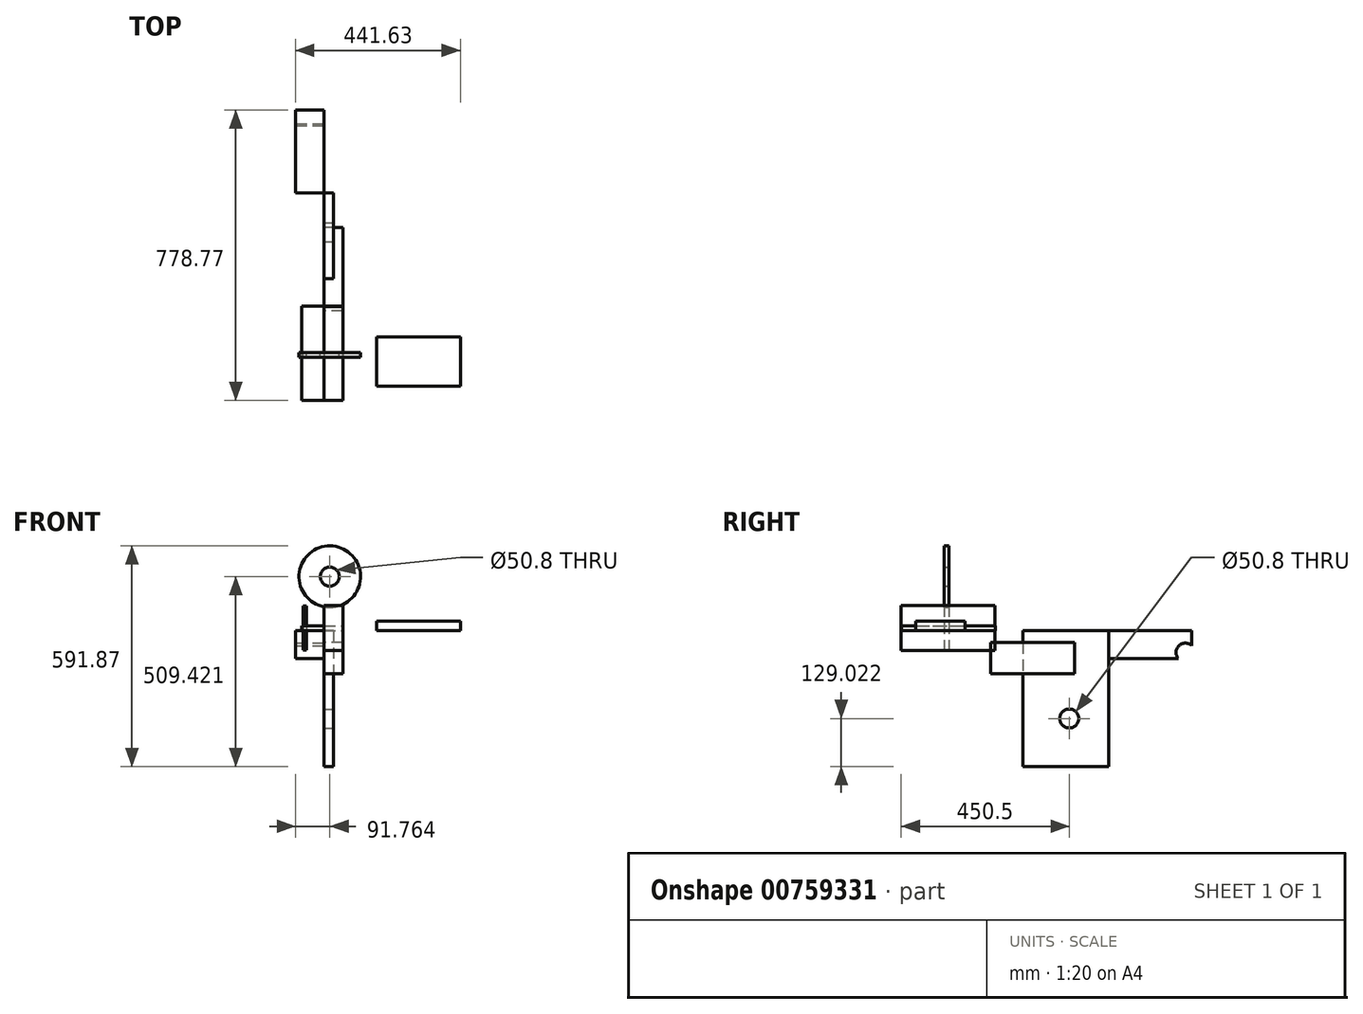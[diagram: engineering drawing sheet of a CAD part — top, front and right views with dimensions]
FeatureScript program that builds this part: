
annotation { "Feature Type Name" : "Feature", "Feature Type Description" : "" }
export const myFeature = defineFeature(function(context is Context, id is Id, definition is map)
    precondition{}
    {
        {
            var Q0;
            Q0=qCreatedBy(makeId("Right.planeOp"),FACE);
            var sketch = newSketch(context, id + "F0", { "sketchPlane" : qUnion([Q0])});
            skLineSegment(sketch, "E0.bottom", {"start": v(123.96, 66.67) * mm, "end": v(-127.95, 66.67) * mm});
            skLineSegment(sketch, "E0.top", {"start": v(123.96, -53.74) * mm, "end": v(-127.95, -53.74) * mm});
            skLineSegment(sketch, "E0.left", {"start": v(123.96, 66.67) * mm, "end": v(123.96, -53.74) * mm});
            skLineSegment(sketch, "E0.right", {"start": v(-127.95, 66.67) * mm, "end": v(-127.95, -53.74) * mm});
            skSolve(sketch);
        }
        {
            var Q0;
            Q0=makeQuery(id+"F0.imprint","IMPRINT",FACE,{"disambiguationData":[TD([[makeQuery(id+"F0.imprint","IMPRINT",EDGE,{"derivedFrom":sQuery(id+"F0.wireOp",EDGE,"E0.bottom")}),1.0]])]});
            extrude(context, id + "F1", {"entities" : qUnion([Q0]), "depth" : 50.8 * mm, "offsetDistance" : 25.4 * mm});
        }
        {
            var Q0;
            Q0=qCreatedBy(makeId("Front.planeOp"),FACE);
            var sketch = newSketch(context, id + "F2", { "sketchPlane" : qUnion([Q0])});
            skLineSegment(sketch, "E1.bottom", {"start": v(-46.48, 66.05) * mm, "end": v(-56.27, 66.05) * mm});
            skLineSegment(sketch, "E1.top", {"start": v(-46.48, -52.52) * mm, "end": v(-56.27, -52.52) * mm});
            skLineSegment(sketch, "E1.left", {"start": v(-46.48, 66.05) * mm, "end": v(-46.48, -52.52) * mm});
            skLineSegment(sketch, "E1.right", {"start": v(-56.27, 66.05) * mm, "end": v(-56.27, -52.52) * mm});
            skSolve(sketch);
        }
        {
            var Q0;
            Q0=makeQuery(id+"F2.imprint","IMPRINT",FACE,{"disambiguationData":[TD([[makeQuery(id+"F2.imprint","IMPRINT",EDGE,{"derivedFrom":sQuery(id+"F2.wireOp",EDGE,"E1.bottom")}),1.0]])]});
            extrude(context, id + "F3", {"entities" : qUnion([Q0]), "depth" : 12.7 * mm, "offsetDistance" : 25.4 * mm});
        }
        {
            var Q0;
            Q0=qCreatedBy(makeId("Front.planeOp"),FACE);
            var sketch = newSketch(context, id + "F4", { "sketchPlane" : qUnion([Q0])});
            skArc(sketch, "E2", {"start": v(-50.02, 64.15) * mm, "mid": v(37.27, 58.21) * mm, "end": v(-28.8, 115.56) * mm});
            skCircle(sketch, "E3", {"center": v(15.56, 144.3) * mm, "radius": 82.45 * mm});
            skSolve(sketch);
        }
        {
            var Q0;
            Q0 = qSketchRegion(id + "F4", true);
            extrude(context, id + "F5", {"entities" : qUnion([Q0]), "depth" : 12.7 * mm, "offsetDistance" : 25.4 * mm});
        }
        {
            var Q0;
            Q0=qCreatedBy(makeId("Top.planeOp"),FACE);
            var sketch = newSketch(context, id + "F6", { "sketchPlane" : qUnion([Q0])});
            skLineSegment(sketch, "E4.bottom", {"start": v(-59.14, -127.5) * mm, "end": v(50.86, -127.5) * mm});
            skLineSegment(sketch, "E4.top", {"start": v(-59.14, 124.15) * mm, "end": v(50.86, 124.15) * mm});
            skLineSegment(sketch, "E4.left", {"start": v(-59.14, -127.5) * mm, "end": v(-59.14, 124.15) * mm});
            skLineSegment(sketch, "E4.right", {"start": v(50.86, -127.5) * mm, "end": v(50.86, 124.15) * mm});
            skSolve(sketch);
        }
        {
            var Q0;
            Q0 = qSketchRegion(id + "F6", true);
            extrude(context, id + "F7", {"entities" : qUnion([Q0]), "depth" : 12.7 * mm, "offsetDistance" : 25.4 * mm});
        }
        {
            var Q0;
            Q0=makeQuery(id+"F5.opExtrude","CAP_FACE",FACE,{"disambiguationData":[OSD([sQuery(id+"F4.wireOp",EDGE,"E3")])],"isStart":true});
            var sketch = newSketch(context, id + "F8", { "sketchPlane" : qUnion([Q0])});
            skPoint(sketch, "E5", {"position": v(-15.56, 144.3) * mm});
            skSolve(sketch);
        }
        {
            var Q0;
            Q0=sQuery(id+"F8.wireOp",VERTEX,"E5");
            var Q1;
            Q1=makeQuery(id+"F5.opExtrude","SWEPT_BODY",BODY,{"disambiguationData":[OSD([sQuery(id+"F4.wireOp",EDGE,"E3")])]});
            hole(context, id + "F9", {"style" : HoleStyle.SIMPLE, "endStyle" : HoleEndStyle.THROUGH, "holeDiameter" : 50.8 * mm, "majorDiameter" : 6.35 * mm, "isTappedThrough" : true, "tappedDepth" : 12.7 * mm, "tapClearance" : 3, "locations" : qUnion([Q0]), "scope" : qUnion([Q1])});
        }
        {
            var Q0;
            Q0=qCreatedBy(makeId("Top.planeOp"),FACE);
            var sketch = newSketch(context, id + "F10", { "sketchPlane" : qUnion([Q0])});
            skLineSegment(sketch, "E6.bottom", {"start": v(140.9, -89.27) * mm, "end": v(365.43, -89.27) * mm});
            skLineSegment(sketch, "E6.top", {"start": v(140.9, 42.8) * mm, "end": v(365.43, 42.8) * mm});
            skLineSegment(sketch, "E6.left", {"start": v(140.9, -89.27) * mm, "end": v(140.9, 42.8) * mm});
            skLineSegment(sketch, "E6.right", {"start": v(365.43, -89.27) * mm, "end": v(365.43, 42.8) * mm});
            skSolve(sketch);
        }
        {
            var Q0;
            Q0=makeQuery(id+"F10.imprint","IMPRINT",FACE,{"disambiguationData":[TD([[makeQuery(id+"F10.imprint","IMPRINT",EDGE,{"derivedFrom":sQuery(id+"F10.wireOp",EDGE,"E6.bottom")}),1.0]])]});
            extrude(context, id + "F11", {"entities" : qUnion([Q0]), "depth" : 25.4 * mm, "offsetDistance" : 25.4 * mm});
        }
        {
            var Q0;
            Q0=qCreatedBy(makeId("Right.planeOp"),FACE);
            var sketch = newSketch(context, id + "F12", { "sketchPlane" : qUnion([Q0])});
            skLineSegment(sketch, "E7.bottom", {"start": v(198.26, 0) * mm, "end": v(427.9, 0) * mm});
            skLineSegment(sketch, "E7.top", {"start": v(198.26, -365.13) * mm, "end": v(427.9, -365.13) * mm});
            skLineSegment(sketch, "E7.left", {"start": v(198.26, 0) * mm, "end": v(198.26, -365.13) * mm});
            skLineSegment(sketch, "E7.right", {"start": v(427.9, 0) * mm, "end": v(427.9, -365.13) * mm});
            skSolve(sketch);
        }
        {
            var Q0;
            Q0=makeQuery(id+"F12.imprint","IMPRINT",FACE,{"disambiguationData":[TD([[makeQuery(id+"F12.imprint","IMPRINT",EDGE,{"derivedFrom":sQuery(id+"F12.wireOp",EDGE,"E7.bottom")}),-1.0]])]});
            extrude(context, id + "F13", {"entities" : qUnion([Q0]), "depth" : 25.4 * mm, "offsetDistance" : 25.4 * mm});
        }
        {
            var Q0;
            Q0=qCreatedBy(makeId("Front.planeOp"),FACE);
            var sketch = newSketch(context, id + "F14", { "sketchPlane" : qUnion([Q0])});
            skArc(sketch, "E8", {"start": v(230.25, 28.07) * mm, "mid": v(123.09, 214.87) * mm, "end": v(38.83, 16.68) * mm});
            skSolve(sketch);
        }
        {
            var Q0;
            Q0=sQuery(id+"F14.wireOp",EDGE,"E8");
            extrude(context, id + "F15", {"bodyType" : ToolBodyType.SURFACE, "surfaceEntities" : qUnion([Q0]), "depth" : 50.8 * mm, "offsetDistance" : 25.4 * mm});
        }
        {
            var Q0;
            Q0=qCreatedBy(makeId("Front.planeOp"),FACE);
            var sketch = newSketch(context, id + "F16", { "sketchPlane" : qUnion([Q0])});
            skArc(sketch, "E9", {"start": v(19.56, 54.99) * mm, "mid": v(-174.04, -384) * mm, "end": v(113.6, 0) * mm});
            skSolve(sketch);
        }
        {
            var Q0;
            Q0=sQuery(id+"F16.wireOp",EDGE,"E9");
            extrude(context, id + "F17", {"bodyType" : ToolBodyType.SURFACE, "surfaceEntities" : qUnion([Q0]), "endBound" : BoundingType.SYMMETRIC, "depth" : 254 * mm, "offsetDistance" : 25.4 * mm});
        }
        {
            var Q0;
            Q0=qCreatedBy(makeId("Right.planeOp"),FACE);
            var sketch = newSketch(context, id + "F18", { "sketchPlane" : qUnion([Q0])});
            skLineSegment(sketch, "E10.bottom", {"start": v(112.33, -32.4) * mm, "end": v(336.19, -32.4) * mm});
            skLineSegment(sketch, "E10.top", {"start": v(112.33, -115.73) * mm, "end": v(336.19, -115.73) * mm});
            skLineSegment(sketch, "E10.left", {"start": v(112.33, -32.4) * mm, "end": v(112.33, -115.73) * mm});
            skLineSegment(sketch, "E10.right", {"start": v(336.19, -32.4) * mm, "end": v(336.19, -115.73) * mm});
            skSolve(sketch);
        }
        {
            var Q0;
            Q0=makeQuery(id+"F18.imprint","IMPRINT",FACE,{"disambiguationData":[TD([[makeQuery(id+"F18.imprint","IMPRINT",EDGE,{"derivedFrom":sQuery(id+"F18.wireOp",EDGE,"E10.bottom")}),-1.0]])]});
            extrude(context, id + "F19", {"entities" : qUnion([Q0]), "depth" : 50.8 * mm, "offsetDistance" : 25.4 * mm});
        }
        {
            var Q0;
            Q0=makeQuery(id+"F13.opExtrude","CAP_FACE",FACE,{"disambiguationData":[OSD([sQuery(id+"F12.wireOp",EDGE,"E7.bottom"),sQuery(id+"F12.wireOp",EDGE,"E7.top"),sQuery(id+"F12.wireOp",EDGE,"E7.left"),sQuery(id+"F12.wireOp",EDGE,"E7.right")])],"isStart":true});
            var sketch = newSketch(context, id + "F20", { "sketchPlane" : qUnion([Q0])});
            skLineSegment(sketch, "E11.bottom", {"start": v(-650.82, -75.63) * mm, "end": v(-204.96, -75.63) * mm});
            skLineSegment(sketch, "E11.top", {"start": v(-650.82, -0.05) * mm, "end": v(-204.96, -0.05) * mm});
            skLineSegment(sketch, "E11.left", {"start": v(-650.82, -75.63) * mm, "end": v(-650.82, -0.05) * mm});
            skLineSegment(sketch, "E11.right", {"start": v(-204.96, -75.63) * mm, "end": v(-204.96, -0.05) * mm});
            skPoint(sketch, "E11.middle", {"position": v(-427.9, -37.84) * mm});
            skSolve(sketch);
        }
        {
            var Q0;
            {var subQ0=sQuery(id+"F20.wireOp",EDGE,"E11.left");Q0=makeQuery(id+"F20.imprint","IMPRINT",FACE,{"disambiguationData":[TD([[makeQuery(id+"F20.imprint","IMPRINT",EDGE,{"derivedFrom":subQ0}),-1.0]])]});}
            extrude(context, id + "F21", {"entities" : qUnion([Q0]), "depth" : 76.2 * mm, "offsetDistance" : 25.4 * mm});
        }
        {
            var Q0;
            Q0=makeQuery(id+"F13.opExtrude","CAP_FACE",FACE,{"disambiguationData":[OSD([sQuery(id+"F12.wireOp",EDGE,"E7.bottom"),sQuery(id+"F12.wireOp",EDGE,"E7.top"),sQuery(id+"F12.wireOp",EDGE,"E7.left"),sQuery(id+"F12.wireOp",EDGE,"E7.right")])],"isStart":false});
            var sketch = newSketch(context, id + "F22", { "sketchPlane" : qUnion([Q0])});
            skPoint(sketch, "E12", {"position": v(322.55, -236.1) * mm});
            skSolve(sketch);
        }
        {
            var Q0;
            Q0=sQuery(id+"F22.wireOp",VERTEX,"E12");
            var Q1;
            Q1=makeQuery(id+"F13.opExtrude","SWEPT_BODY",BODY,{"disambiguationData":[OSD([sQuery(id+"F12.wireOp",EDGE,"E7.bottom"),sQuery(id+"F12.wireOp",EDGE,"E7.top"),sQuery(id+"F12.wireOp",EDGE,"E7.left"),sQuery(id+"F12.wireOp",EDGE,"E7.right")])]});
            hole(context, id + "F23", {"style" : HoleStyle.SIMPLE, "endStyle" : HoleEndStyle.THROUGH, "holeDiameter" : 50.8 * mm, "majorDiameter" : 6.35 * mm, "isTappedThrough" : true, "tappedDepth" : 12.7 * mm, "tapClearance" : 3, "locations" : qUnion([Q0]), "scope" : qUnion([Q1])});
        }
        {
            var Q0;
            Q0=makeQuery(id+"F21.opExtrude","CAP_FACE",FACE,{"disambiguationData":[OSD([sQuery(id+"F12.wireOp",EDGE,"E7.right"),sQuery(id+"F20.wireOp",EDGE,"E11.bottom"),sQuery(id+"F20.wireOp",EDGE,"E11.top"),sQuery(id+"F20.wireOp",EDGE,"E11.left")])],"isStart":true});
            var sketch = newSketch(context, id + "F24", { "sketchPlane" : qUnion([Q0])});
            skPoint(sketch, "E13", {"position": v(633.74, -59.33) * mm});
            skSolve(sketch);
        }
        {
            var Q0;
            Q0=sQuery(id+"F24.wireOp",VERTEX,"E13");
            var Q1;
            Q1=makeQuery(id+"F21.opExtrude","SWEPT_BODY",BODY,{"disambiguationData":[OSD([sQuery(id+"F12.wireOp",EDGE,"E7.right"),sQuery(id+"F20.wireOp",EDGE,"E11.bottom"),sQuery(id+"F20.wireOp",EDGE,"E11.top"),sQuery(id+"F20.wireOp",EDGE,"E11.left")])]});
            hole(context, id + "F25", {"style" : HoleStyle.SIMPLE, "endStyle" : HoleEndStyle.THROUGH, "holeDiameter" : 50.8 * mm, "majorDiameter" : 6.35 * mm, "isTappedThrough" : true, "tappedDepth" : 12.7 * mm, "tapClearance" : 3, "locations" : qUnion([Q0]), "scope" : qUnion([Q1])});
        }
    });
